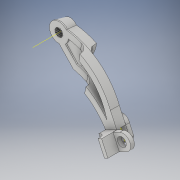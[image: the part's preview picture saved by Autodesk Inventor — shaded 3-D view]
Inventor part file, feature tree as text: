
AUTODESK INVENTOR PART (.ipt)
format: ipt  version: 2018 (Build 220112000, 112)  size: 462,848 bytes
history: native  units: in
note: dims shown in document units (in); Inventor stores cm internally (conversion verified against a paired STEP export)
features: sketch x15, extrude x12, fillet x2, plane x1, other x1, pattern_circular x1
ambient origin geometry x8: Origin, YZ Plane, XZ Plane, XY Plane, X Axis, Y Axis, Z Axis, Center Point
bodies: Solid1 (feature_tree)
feature tree (32):
  sketch  "Sketch1"  dims[d15=1.0in d47=0.1969in d48=0.1969in]
  extrude  "Extrusion12"  Depth=0.1969in
  sketch  "Sketch16"  dims[d63=2.1654in d64=0.1969in]
  extrude  "Extrusion16"  Depth=0.1969in
  extrude  "Extrusion19"  Depth=0.1969in
  plane  "Work Plane9"
  sketch  "Sketch25"  dims[d75=0.2559in d76=0.2756in d77=0.0in]
  sketch  "Sketch26"  dims[d101=0.1181in d102=0.3937in d103=0.0in d106=0.5906in]
  extrude  "Extrusion20"  Depth=0.1969in
  sketch  "Sketch30"  dims[d118=0.4724in d119=0.1181in]
  extrude  "Extrusion21"  Depth=0.2756in TaperAngle=0.0deg
  extrude  "Extrusion22"  Depth=0.3937in TaperAngle=0.0deg
  fillet  "Fillet5"  Radius=0.5906in
  extrude  "Extrusion25"  Depth=0.1575in TaperAngle=0.0deg
  extrude  "Extrusion26"  Depth=0.1181in
  extrude  "Extrusion27"  Depth=0.2165in
  extrude  "Extrusion29"  Depth=0.315in TaperAngle=0.0deg
  fillet  "Fillet10"  Radius=0.2362in
  extrude  "Extrusion31"  Depth=0.2362in
  extrude  "Extrusion32"  Depth=0.4724in TaperAngle=0.0deg
  other  "Work Axis1"
  pattern_circular  "Circular Pattern1"  [2 undecoded]
  sketch  "Sketch19"  dims[d65=0.1969in d66=0.7874in]
  sketch  "Sketch24"  dims[d68=0.1969in d74=0.1969in]
  sketch  "Sketch27"  dims[d115=0.5906in d116=0.1575in d117=0.0in]
  sketch  "Sketch31"  dims[d120=0.374in d121=0.2165in]
  sketch  "Sketch32"  dims[d122=0.2362in d123=0.315in d124=0.0in d129=0.2362in]
  sketch  "Sketch35"  dims[d130=0.1181in d131=0.2362in]
  sketch  "Sketch37"  dims[d132=0.1181in d133=0.4724in d134=0.0in]
  sketch  "Sketch39"  dims[d135=0.1516in d136=0.0in]
  sketch  "Sketch41"  dims[d139=0.1969in]
  sketch  "Sketch42"  dims[d140=0.2756in d141=0.1181in d142=0.0in d143=0.2362in d153=0.2756in d154=0.0in d155=0.1181in d156=0.0in d157=1.7717in d158=0.2362in d159=0.0in d166=1.7717in d167=0.315in d168=-0.0893in d178=0.1181in d179=0.1575in d180=0.1378in d184=0.3543in d185=0.0in d190=0.0236in d191=0.0098in d192=0.0197in d194=0.0079in d195=0.0079in d196=0.0197in d197=0.0197in d198=0.3543in d199=0.0in d200=7.0866in d201=360.0deg d203=0.1969in]
note: 2 required parameter values undecoded (feature->parameter linkage not recoverable at this tier; creation-order binding heuristic only, values carry confidence <= 0.55)
